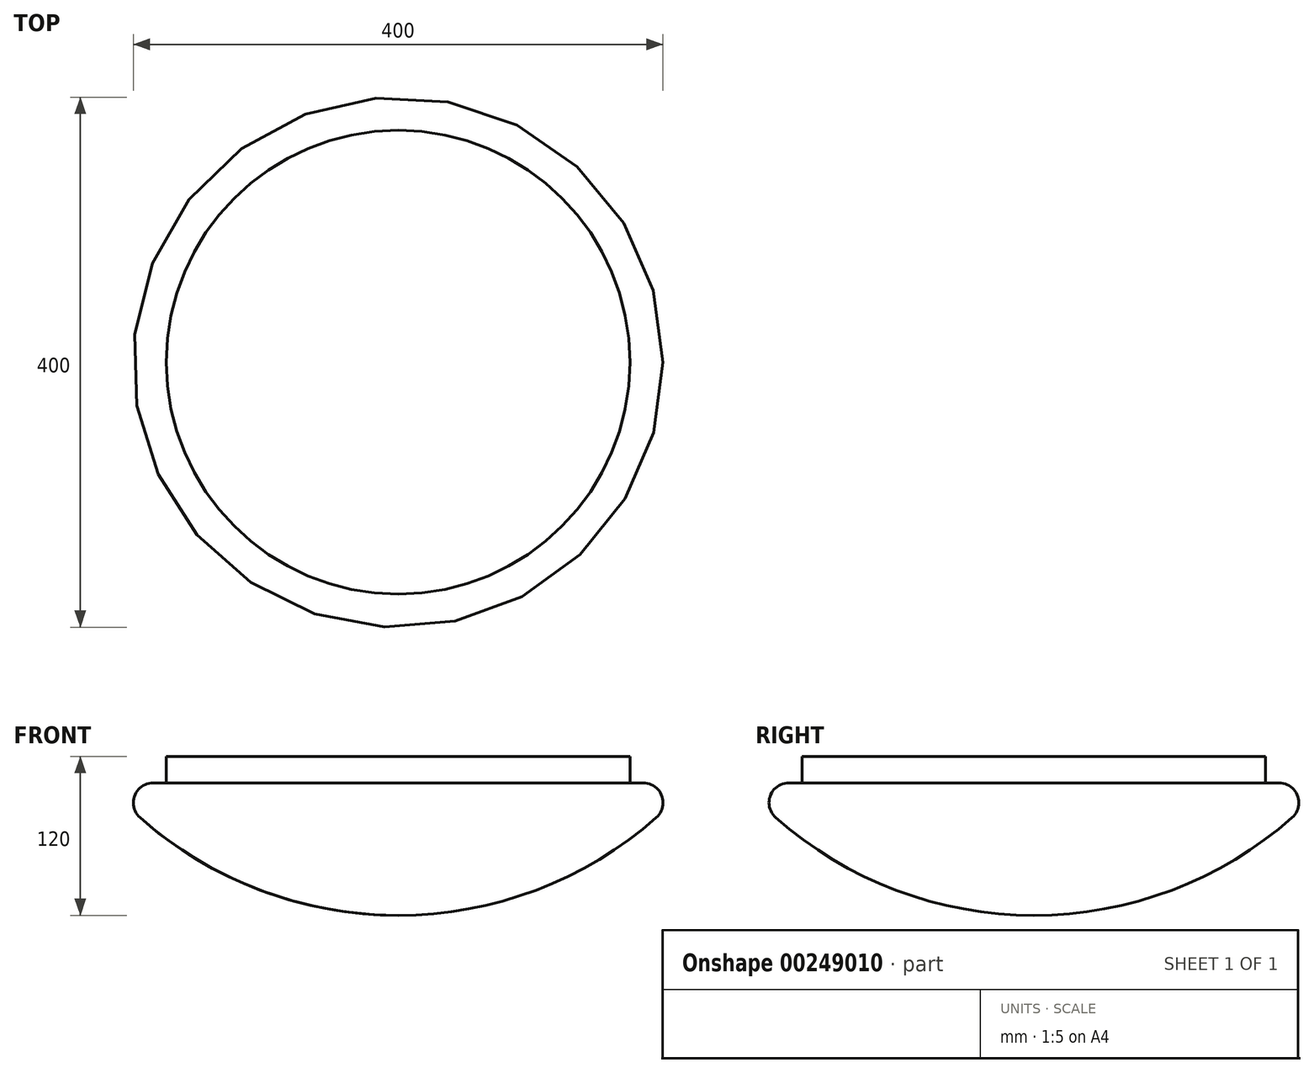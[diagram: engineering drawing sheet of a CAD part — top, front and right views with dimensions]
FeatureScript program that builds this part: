
annotation { "Feature Type Name" : "Feature", "Feature Type Description" : "" }
export const myFeature = defineFeature(function(context is Context, id is Id, definition is map)
    precondition{}
    {
        {
            var Q0;
            Q0=qCreatedBy(makeId("Front.planeOp"),FACE);
            var sketch = newSketch(context, id + "F0", { "sketchPlane" : qUnion([Q0])});
            skLineSegment(sketch, "E0", {"start": v(0, 0) * mm, "end": v(-175, 0) * mm});
            skLineSegment(sketch, "E1", {"start": v(-175, 0) * mm, "end": v(-175, -20) * mm});
            skLineSegment(sketch, "E2", {"start": v(-175, -20) * mm, "end": v(-185, -20) * mm});
            skArc(sketch, "E3", {"start": v(-185, -20) * mm, "mid": v(-199.03, -29.7) * mm, "end": v(-194.93, -46.24) * mm});
            skLineSegment(sketch, "E4.MirrorCS", {"start": v(175, 0) * mm, "end": v(175, -20) * mm});
            skArc(sketch, "E5.MirrorCS", {"start": v(185, -20) * mm, "mid": v(199.03, -29.7) * mm, "end": v(194.93, -46.24) * mm});
            skLineSegment(sketch, "E6.MirrorCS", {"start": v(0, 0) * mm, "end": v(175, 0) * mm});
            skLineSegment(sketch, "E7.MirrorCS", {"start": v(175, -20) * mm, "end": v(185, -20) * mm});
            skArc(sketch, "E8", {"start": v(-194.93, -46.24) * mm, "mid": v(0, -120) * mm, "end": v(194.93, -46.24) * mm});
            skPoint(sketch, "E9.orphan", {"position": v(-185, -50) * mm});
            skPoint(sketch, "E10.orphan", {"position": v(185, -50) * mm});
            skLineSegment(sketch, "E11", {"start": v(-194.93, -46.24) * mm, "end": v(194.93, -46.24) * mm, "construction": true});
            skLineSegment(sketch, "E12", {"start": v(0, -2.62) * mm, "end": v(0, -120) * mm});
            skSolve(sketch);
        }
        {
            var Q0;
            Q0=qCreatedBy(makeId("Front.planeOp"),FACE);
            var sketch = newSketch(context, id + "F1", { "sketchPlane" : qUnion([Q0])});
            skLineSegment(sketch, "E13.0", {"start": v(0, 0) * mm, "end": v(0, -120) * mm});
            skLineSegment(sketch, "E14.0", {"start": v(0, 0) * mm, "end": v(-175, 0) * mm});
            skArc(sketch, "E15.0", {"start": v(-194.93, -46.24) * mm, "mid": v(-104.2, -100.94) * mm, "end": v(0, -120) * mm});
            skArc(sketch, "E16.0", {"start": v(-185, -20) * mm, "mid": v(-199.03, -29.7) * mm, "end": v(-194.93, -46.24) * mm});
            skLineSegment(sketch, "E17.0", {"start": v(-175, -20) * mm, "end": v(-185, -20) * mm});
            skLineSegment(sketch, "E18.0", {"start": v(-175, 0) * mm, "end": v(-175, -20) * mm});
            skPoint(sketch, "E19.orphan", {"position": v(194.93, -46.24) * mm});
            skPoint(sketch, "E20.orphan", {"position": v(0, -2.62) * mm});
            skSolve(sketch);
        }
        {
            var Q0;
            Q0=makeQuery(id+"F1.imprint","IMPRINT",FACE,{"disambiguationData":[TD([[makeQuery(id+"F1.imprint","IMPRINT",EDGE,{"derivedFrom":sQuery(id+"F1.wireOp",EDGE,"E13.0")}),-1.0]])]});
            var Q1;
            Q1=sQuery(id+"F1.wireOp",EDGE,"E13.0");
            revolve(context, id + "F2", {"entities" : qUnion([Q0]), "axis" : qUnion([Q1]), "revolveType" : RevolveType.FULL});
        }
    });
